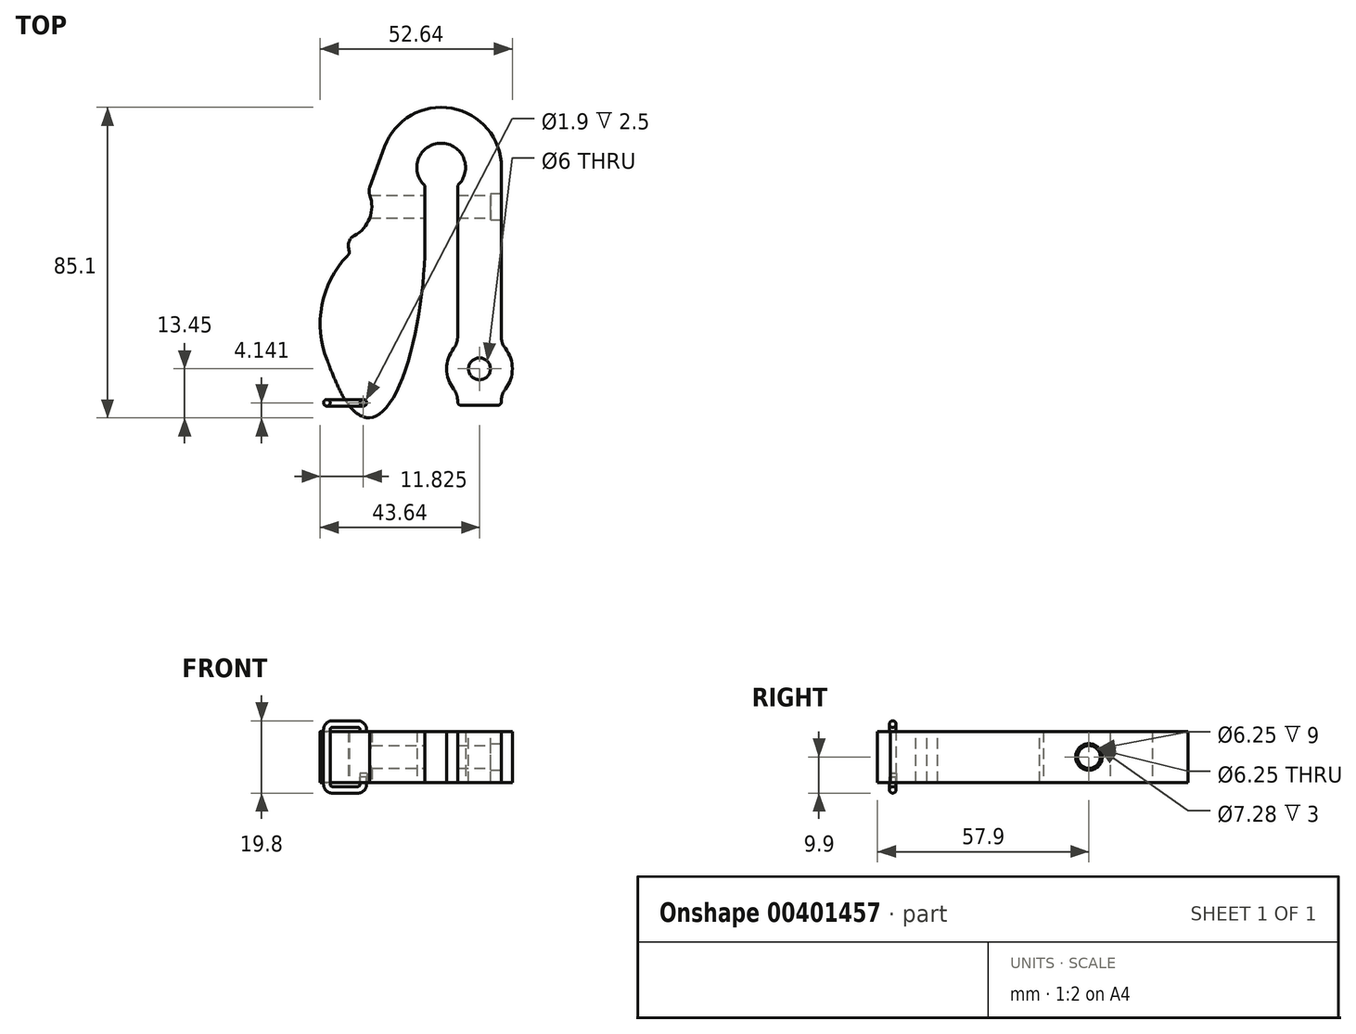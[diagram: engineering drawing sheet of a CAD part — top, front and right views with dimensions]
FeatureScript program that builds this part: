
annotation { "Feature Type Name" : "Feature", "Feature Type Description" : "" }
export const myFeature = defineFeature(function(context is Context, id is Id, definition is map)
    precondition{}
    {
        {
            var Q0;
            Q0=qCreatedBy(makeId("Top.planeOp"),FACE);
            var sketch = newSketch(context, id + "F0", { "sketchPlane" : qUnion([Q0])});
            skCircle(sketch, "E0", {"center": v(0, 0) * mm, "radius": 16.5 * mm, "construction": true});
            skCircle(sketch, "E1", {"center": v(0, 0) * mm, "radius": 6.68 * mm, "construction": true});
            skLineSegment(sketch, "E2.bottom", {"start": v(16.5, 0) * mm, "end": v(4.5, 0) * mm, "construction": true});
            skLineSegment(sketch, "E2.top", {"start": v(16.5, -65.15) * mm, "end": v(4.5, -65.15) * mm, "construction": true});
            skLineSegment(sketch, "E2.left", {"start": v(16.5, 0) * mm, "end": v(16.5, -65.15) * mm, "construction": true});
            skLineSegment(sketch, "E2.right", {"start": v(4.5, 0) * mm, "end": v(4.5, -65.15) * mm, "construction": true});
            skLineSegment(sketch, "E3.bottom", {"start": v(-16.5, 0) * mm, "end": v(-3.67, 0) * mm, "construction": true});
            skLineSegment(sketch, "E4.MirrorCS", {"start": v(-4.5, 0) * mm, "end": v(-4.5, -65.15) * mm, "construction": true});
            skLineSegment(sketch, "E5.MirrorCS", {"start": v(-16.5, 0) * mm, "end": v(-16.5, -65.15) * mm, "construction": true});
            skLineSegment(sketch, "E6.MirrorCS", {"start": v(-16.5, -65.15) * mm, "end": v(-4.5, -65.15) * mm, "construction": true});
            skLineSegment(sketch, "E7", {"start": v(0, 16.5) * mm, "end": v(-40, 16.5) * mm, "construction": true});
            skLineSegment(sketch, "E8", {"start": v(-35.1, 16.5) * mm, "end": v(-35.1, -10.7) * mm, "construction": true});
            skLineSegment(sketch, "E9", {"start": v(-35.1, -10.7) * mm, "end": v(24.91, -10.7) * mm, "construction": true});
            skArc(sketch, "E10", {"start": v(-34.47, -76.44) * mm, "mid": v(-14.3, -71.83) * mm, "end": v(-4.5, -53.6) * mm, "construction": true});
            skPoint(sketch, "E11", {"position": v(-34.47, -76.44) * mm});
            skLineSegment(sketch, "E12", {"start": v(-30, -57) * mm, "end": v(-10.83, -57) * mm, "construction": true});
            skArc(sketch, "E13", {"start": v(-25.7, -24.2) * mm, "mid": v(-32.7, -37.96) * mm, "end": v(-31.02, -53.3) * mm, "construction": true});
            skLineSegment(sketch, "E14", {"start": v(-35.28, -13.7) * mm, "end": v(24.91, -13.7) * mm, "construction": true});
            skLineSegment(sketch, "E15", {"start": v(24.64, -7.7) * mm, "end": v(-35.1, -7.7) * mm, "construction": true});
            skCircle(sketch, "E16", {"center": v(-28, -10.7) * mm, "radius": 9 * mm, "construction": true});
            skLineSegment(sketch, "E17", {"start": v(-20, 5.87) * mm, "end": v(-20, -31.3) * mm, "construction": true});
            skLineSegment(sketch, "E18", {"start": v(-20, -6.58) * mm, "end": v(-15.49, 5.7) * mm, "construction": true});
            skLineSegment(sketch, "E19", {"start": v(-25.7, -15.52) * mm, "end": v(-25.7, -32.88) * mm, "construction": true});
            skLineSegment(sketch, "E20", {"start": v(-37.42, -24.2) * mm, "end": v(-13.09, -24.2) * mm, "construction": true});
            skCircle(sketch, "E21", {"center": v(-60.5, -65.75) * mm, "radius": 32 * mm, "construction": true});
            skPoint(sketch, "E22", {"position": v(-25.7, -24.2) * mm});
            skSolve(sketch);
        }
        {
            var Q0;
            Q0=qCreatedBy(makeId("Top.planeOp"),FACE);
            var sketch = newSketch(context, id + "F1", { "sketchPlane" : qUnion([Q0])});
            skLineSegment(sketch, "E23", {"start": v(-20, -6.58) * mm, "end": v(-15.49, 5.7) * mm});
            skArc(sketch, "E24", {"start": v(-15.49, 5.7) * mm, "mid": v(2.9, 16.24) * mm, "end": v(16.5, 0) * mm});
            skLineSegment(sketch, "E25", {"start": v(16.5, 0) * mm, "end": v(16.5, -65.15) * mm});
            skLineSegment(sketch, "E26", {"start": v(16.5, -65.15) * mm, "end": v(4.5, -65.15) * mm});
            skLineSegment(sketch, "E27", {"start": v(4.5, -65.15) * mm, "end": v(4.5, -4.93) * mm});
            skArc(sketch, "E28", {"start": v(4.5, -4.93) * mm, "mid": v(0, 6.68) * mm, "end": v(-4.5, -4.93) * mm});
            skLineSegment(sketch, "E29", {"start": v(-4.5, -4.93) * mm, "end": v(-4.5, -46.93) * mm});
            skArc(sketch, "E30", {"start": v(-31.18, -52.92) * mm, "mid": v(-32.66, -37.75) * mm, "end": v(-25.7, -24.2) * mm});
            skArc(sketch, "E31", {"start": v(-25.7, -19.4) * mm, "mid": v(-19.78, -14.36) * mm, "end": v(-20, -6.58) * mm});
            skPoint(sketch, "E32", {"position": v(-28.4, -71.45) * mm});
            skArc(sketch, "E33", {"start": v(-28.4, -71.45) * mm, "mid": v(-11.46, -64.05) * mm, "end": v(-4.5, -46.93) * mm});
            skArc(sketch, "E34", {"start": v(-31.18, -52.92) * mm, "mid": v(-28.7, -62.02) * mm, "end": v(-28.4, -71.45) * mm});
            skLineSegment(sketch, "E35", {"start": v(-25.7, -19.4) * mm, "end": v(-25.23, -23.14) * mm});
            skFitSpline(sketch, "E36", {"points": [v(-25.23, -23.14) * mm, v(-25.7, -24.2) * mm], "startDerivative": vector(0.3, -1.7) * mm, "endDerivative": vector(-0.99, -1.09) * mm});
            skSolve(sketch);
        }
        {
            var Q0;
            Q0=makeQuery(id+"F1.imprint","IMPRINT",FACE,{"disambiguationData":[TD([[makeQuery(id+"F1.imprint","IMPRINT",EDGE,{"derivedFrom":sQuery(id+"F1.wireOp",EDGE,"E23")}),-1.0]])]});
            extrude(context, id + "F2", {"entities" : qUnion([Q0]), "depth" : 14 * mm});
        }
        {
            var Q0;
            Q0=makeQuery(id+"F2.opExtrude","SWEPT_FACE",FACE,{"disambiguationData":[OSD([sQuery(id+"F1.wireOp",EDGE,"E25")])]});
            var sketch = newSketch(context, id + "F3", { "sketchPlane" : qUnion([Q0])});
            skCircle(sketch, "E37", {"center": v(-10.7, 7) * mm, "radius": 3.12 * mm});
            skSolve(sketch);
        }
        {
            var Q0;
            Q0=qSketchRegion(id+"F3",true);
            extrude(context, id + "F4", {"entities" : qUnion([Q0]), "operationType" : NewBodyOperationType.REMOVE, "endBound" : BoundingType.THROUGH_ALL, "oppositeDirection" : true, "depth" : 25 * mm});
        }
        {
            var Q0;
            Q0=makeQuery(id+"F2.opExtrude","SWEPT_EDGE",EDGE,{"disambiguationData":[OSD([sQuery(id+"F1.wireOp",EDGE,"iYDEJ3TL-iV67-zqoH-FoCL-mFiRr5Qzbk3r"),sQuery(id+"F1.wireOp",EDGE,"E31")])]});
            fillet(context, id + "F5", {"entities" : qUnion([Q0]), "radius" : 3 * mm, "tangentPropagation" : true, "allowEdgeOverflow" : false});
        }
        {
            var Q0;
            Q0=makeQuery(id+"F2.opExtrude","SWEPT_EDGE",EDGE,{"disambiguationData":[OSD([sQuery(id+"F1.wireOp",EDGE,"E30"),sQuery(id+"F1.wireOp",EDGE,"iYDEJ3TL-iV67-zqoH-FoCL-mFiRr5Qzbk3r")])]});
            fillet(context, id + "F6", {"entities" : qUnion([Q0]), "radius" : 2 * mm, "tangentPropagation" : true, "allowEdgeOverflow" : false});
        }
        {
            var Q0;
            Q0=makeQuery(id+"F2.opExtrude","SWEPT_EDGE",EDGE,{"disambiguationData":[OSD([sQuery(id+"F1.wireOp",EDGE,"E33"),sQuery(id+"F1.wireOp",EDGE,"Xg7VqQur-UJu3-oRoY-WVdC-1TGSa8gNUCBY")])]});
            fillet(context, id + "F7", {"entities" : qUnion([Q0]), "radius" : 5 * mm, "tangentPropagation" : true, "allowEdgeOverflow" : false});
        }
        {
            var Q0;
            Q0=makeQuery(id+"F2.opExtrude","CAP_FACE",FACE,{"disambiguationData":[OSD([sQuery(id+"F1.wireOp",EDGE,"E23"),sQuery(id+"F1.wireOp",EDGE,"E24"),sQuery(id+"F1.wireOp",EDGE,"E25"),sQuery(id+"F1.wireOp",EDGE,"E26"),sQuery(id+"F1.wireOp",EDGE,"E27"),sQuery(id+"F1.wireOp",EDGE,"E28"),sQuery(id+"F1.wireOp",EDGE,"E29"),sQuery(id+"F1.wireOp",EDGE,"E30"),sQuery(id+"F1.wireOp",EDGE,"iYDEJ3TL-iV67-zqoH-FoCL-mFiRr5Qzbk3r"),sQuery(id+"F1.wireOp",EDGE,"E31"),sQuery(id+"F1.wireOp",EDGE,"E33"),sQuery(id+"F1.wireOp",EDGE,"Xg7VqQur-UJu3-oRoY-WVdC-1TGSa8gNUCBY")])],"isStart":false});
            var sketch = newSketch(context, id + "F8", { "sketchPlane" : qUnion([Q0])});
            skCircle(sketch, "E38", {"center": v(10.5, -55.15) * mm, "radius": 3 * mm});
            skPoint(sketch, "E39.middle", {"position": v(10.5, -58.15) * mm});
            skSolve(sketch);
        }
        {
            var Q0;
            Q0=makeQuery(id+"F0fC8d2KKsZCDmL_1.boolean.opBoolean","COPY",EDGE,{"derivedFrom":makeQuery(id+"F0fC8d2KKsZCDmL_1.opExtrude","CAP_EDGE",EDGE,{"disambiguationData":[OSD([sQuery(id+"F8.wireOp",EDGE,"E39.left")])],"isStart":true})});
            var Q1;
            Q1=makeQuery(id+"F0fC8d2KKsZCDmL_1.boolean.opBoolean","COPY",EDGE,{"derivedFrom":makeQuery(id+"F0fC8d2KKsZCDmL_1.opExtrude","CAP_EDGE",EDGE,{"disambiguationData":[OSD([sQuery(id+"F8.wireOp",EDGE,"E38")])],"isStart":true})});
            var Q2;
            Q2=makeQuery(id+"F2.opExtrude","SWEPT_EDGE",EDGE,{"disambiguationData":[OSD([sQuery(id+"F1.wireOp",EDGE,"E26"),sQuery(id+"F1.wireOp",EDGE,"E27")])]});
            var Q3;
            Q3=makeQuery(id+"F2.opExtrude","SWEPT_EDGE",EDGE,{"disambiguationData":[OSD([sQuery(id+"F1.wireOp",EDGE,"E25"),sQuery(id+"F1.wireOp",EDGE,"E26")])]});
            var Q4;
            Q4=makeQuery(id+"F0fC8d2KKsZCDmL_1.boolean.opBoolean","INTERSECT",EDGE,{"derivedFrom":[makeQuery(id+"F2.opExtrude","CAP_FACE",FACE,{"disambiguationData":[OSD([sQuery(id+"F1.wireOp",EDGE,"E23"),sQuery(id+"F1.wireOp",EDGE,"E24"),sQuery(id+"F1.wireOp",EDGE,"E25"),sQuery(id+"F1.wireOp",EDGE,"E26"),sQuery(id+"F1.wireOp",EDGE,"E27"),sQuery(id+"F1.wireOp",EDGE,"E28"),sQuery(id+"F1.wireOp",EDGE,"E29"),sQuery(id+"F1.wireOp",EDGE,"E30"),sQuery(id+"F1.wireOp",EDGE,"iYDEJ3TL-iV67-zqoH-FoCL-mFiRr5Qzbk3r"),sQuery(id+"F1.wireOp",EDGE,"E31"),sQuery(id+"F1.wireOp",EDGE,"E33"),sQuery(id+"F1.wireOp",EDGE,"Xg7VqQur-UJu3-oRoY-WVdC-1TGSa8gNUCBY")])],"isStart":true}),makeQuery(id+"F0fC8d2KKsZCDmL_1.opExtrude","SWEPT_FACE",FACE,{"disambiguationData":[OSD([sQuery(id+"F8.wireOp",EDGE,"E39.right")])]})]});
            fillet(context, id + "F9", {"entities" : qUnion([Q0, Q1, Q2, Q3, Q4]), "radius" : 1 * mm, "tangentPropagation" : true, "allowEdgeOverflow" : false});
        }
        {
            var Q0;
            Q0=qCreatedBy(makeId("Top.planeOp"),FACE);
            var sketch = newSketch(context, id + "F10", { "sketchPlane" : qUnion([Q0])});
            skLineSegment(sketch, "E40", {"start": v(-5.9, -69.53) * mm, "end": v(-56.37, -69.53) * mm, "construction": true});
            skLineSegment(sketch, "E41", {"start": v(-56.43, -70.53) * mm, "end": v(-5.7, -70.53) * mm, "construction": true});
            skLineSegment(sketch, "E42", {"start": v(-27.31, -50.14) * mm, "end": v(-27.31, -74.97) * mm, "construction": true});
            skLineSegment(sketch, "E43", {"start": v(-28.31, -50.14) * mm, "end": v(-28.31, -74.79) * mm, "construction": true});
            skLineSegment(sketch, "E44", {"start": v(-21.31, -51.33) * mm, "end": v(-21.31, -64.46) * mm, "construction": true});
            skLineSegment(sketch, "E45", {"start": v(-32.6, -67.53) * mm, "end": v(-13.03, -67.53) * mm, "construction": true});
            skCircle(sketch, "E46", {"center": v(-21.31, -64.46) * mm, "radius": 0.95 * mm});
            skArc(sketch, "E47", {"start": v(-29.98, -59.47) * mm, "mid": v(-25, -73.75) * mm, "end": v(-11.59, -66.78) * mm, "construction": true});
            skSolve(sketch);
        }
        {
            var Q0;
            Q0=qSketchRegion(id+"F10",true);
            extrude(context, id + "F11", {"entities" : qUnion([Q0]), "operationType" : NewBodyOperationType.REMOVE, "depth" : 1.5 * mm});
        }
        {
            var Q0;
            Q0=makeQuery(id+"F2.opExtrude","CAP_FACE",FACE,{"disambiguationData":[OSD([sQuery(id+"F1.wireOp",EDGE,"E23"),sQuery(id+"F1.wireOp",EDGE,"E24"),sQuery(id+"F1.wireOp",EDGE,"E25"),sQuery(id+"F1.wireOp",EDGE,"E26"),sQuery(id+"F1.wireOp",EDGE,"E27"),sQuery(id+"F1.wireOp",EDGE,"E28"),sQuery(id+"F1.wireOp",EDGE,"E29"),sQuery(id+"F1.wireOp",EDGE,"E30"),sQuery(id+"F1.wireOp",EDGE,"iYDEJ3TL-iV67-zqoH-FoCL-mFiRr5Qzbk3r"),sQuery(id+"F1.wireOp",EDGE,"E31"),sQuery(id+"F1.wireOp",EDGE,"E33"),sQuery(id+"F1.wireOp",EDGE,"Xg7VqQur-UJu3-oRoY-WVdC-1TGSa8gNUCBY")])],"isStart":false});
            var sketch = newSketch(context, id + "F12", { "sketchPlane" : qUnion([Q0])});
            skCircle(sketch, "E48", {"center": v(-21.31, -64.46) * mm, "radius": 0.9 * mm});
            skSolve(sketch);
        }
        {
            var Q0;
            Q0=qSketchRegion(id+"F12",true);
            extrude(context, id + "F13", {"entities" : qUnion([Q0]), "operationType" : NewBodyOperationType.REMOVE, "oppositeDirection" : true, "depth" : 2.5 * mm});
        }
        {
            var Q0;
            Q0=makeQuery(id+"F2.opExtrude","CAP_FACE",FACE,{"disambiguationData":[OSD([sQuery(id+"F1.wireOp",EDGE,"E23"),sQuery(id+"F1.wireOp",EDGE,"E24"),sQuery(id+"F1.wireOp",EDGE,"E25"),sQuery(id+"F1.wireOp",EDGE,"E26"),sQuery(id+"F1.wireOp",EDGE,"E27"),sQuery(id+"F1.wireOp",EDGE,"E28"),sQuery(id+"F1.wireOp",EDGE,"E29"),sQuery(id+"F1.wireOp",EDGE,"E30"),sQuery(id+"F1.wireOp",EDGE,"iYDEJ3TL-iV67-zqoH-FoCL-mFiRr5Qzbk3r"),sQuery(id+"F1.wireOp",EDGE,"E31"),sQuery(id+"F1.wireOp",EDGE,"E33"),sQuery(id+"F1.wireOp",EDGE,"Xg7VqQur-UJu3-oRoY-WVdC-1TGSa8gNUCBY")])],"isStart":false});
            cPlane(context, id + "F14", {"entities" : qUnion([Q0]), "cplaneType" : CPlaneType.OFFSET, "offset" : 4 * mm, "oppositeDirection" : true, "width" : 150 * mm, "height" : 150 * mm});
        }
        {
            var Q0;
            Q0=qCreatedBy(id+"F14.planeOp",FACE);
            cPlane(context, id + "F15", {"entities" : qUnion([Q0]), "cplaneType" : CPlaneType.OFFSET, "offset" : 6 * mm, "oppositeDirection" : true, "width" : 150 * mm, "height" : 150 * mm});
        }
        {
            var Q0;
            Q0=makeQuery(id+"F3.imprint","IMPRINT",FACE,{"disambiguationData":[TD([[makeQuery(id+"F3.imprint","IMPRINT",EDGE,{"derivedFrom":sQuery(id+"F3.wireOp",EDGE,"E37")}),-1.0]])]});
            var sketch = newSketch(context, id + "F16", { "sketchPlane" : qUnion([Q0])});
            skCircle(sketch, "E49", {"center": v(-10.7, 7) * mm, "radius": 3.64 * mm});
            skSolve(sketch);
        }
        {
            var Q0;
            Q0=qSketchRegion(id+"F16",true);
            extrude(context, id + "F17", {"entities" : qUnion([Q0]), "operationType" : NewBodyOperationType.REMOVE, "oppositeDirection" : true, "depth" : 3 * mm});
        }
        {
            var Q0;
            Q0=makeQuery(id+"F2.opExtrude","CAP_FACE",FACE,{"disambiguationData":[OSD([sQuery(id+"F1.wireOp",EDGE,"E23"),sQuery(id+"F1.wireOp",EDGE,"E24"),sQuery(id+"F1.wireOp",EDGE,"E25"),sQuery(id+"F1.wireOp",EDGE,"E26"),sQuery(id+"F1.wireOp",EDGE,"E27"),sQuery(id+"F1.wireOp",EDGE,"E28"),sQuery(id+"F1.wireOp",EDGE,"E29"),sQuery(id+"F1.wireOp",EDGE,"E30"),sQuery(id+"F1.wireOp",EDGE,"iYDEJ3TL-iV67-zqoH-FoCL-mFiRr5Qzbk3r"),sQuery(id+"F1.wireOp",EDGE,"E31"),sQuery(id+"F1.wireOp",EDGE,"E33"),sQuery(id+"F1.wireOp",EDGE,"E34")])],"isStart":false});
            var sketch = newSketch(context, id + "F18", { "sketchPlane" : qUnion([Q0])});
            skFitSpline(sketch, "E50", {"points": [v(-30.37, -55.1) * mm, v(-24.1, -66.53) * mm, v(-14.21, -66.47) * mm], "startDerivative": vector(8.93, -20.6) * mm, "endDerivative": vector(25.63, 20.5) * mm});
            skLineSegment(sketch, "E51", {"start": v(-30.37, -55.1) * mm, "end": v(-30.37, -71.38) * mm});
            skLineSegment(sketch, "E52", {"start": v(-30.37, -71.38) * mm, "end": v(-14.21, -71.38) * mm});
            skLineSegment(sketch, "E53", {"start": v(-14.21, -71.38) * mm, "end": v(-14.21, -66.47) * mm});
            skSolve(sketch);
        }
        {
            var Q0;
            Q0=qSketchRegion(id+"F18",true);
            extrude(context, id + "F19", {"entities" : qUnion([Q0]), "operationType" : NewBodyOperationType.REMOVE, "endBound" : BoundingType.THROUGH_ALL, "oppositeDirection" : true, "depth" : 25 * mm});
        }
        {
            var Q0;
            Q0=makeQuery(id+"F2.opExtrude","CAP_FACE",FACE,{"disambiguationData":[OSD([sQuery(id+"F1.wireOp",EDGE,"E23"),sQuery(id+"F1.wireOp",EDGE,"E24"),sQuery(id+"F1.wireOp",EDGE,"E25"),sQuery(id+"F1.wireOp",EDGE,"E26"),sQuery(id+"F1.wireOp",EDGE,"E27"),sQuery(id+"F1.wireOp",EDGE,"E28"),sQuery(id+"F1.wireOp",EDGE,"E29"),sQuery(id+"F1.wireOp",EDGE,"E30"),sQuery(id+"F1.wireOp",EDGE,"iYDEJ3TL-iV67-zqoH-FoCL-mFiRr5Qzbk3r"),sQuery(id+"F1.wireOp",EDGE,"E31"),sQuery(id+"F1.wireOp",EDGE,"E33"),sQuery(id+"F1.wireOp",EDGE,"E34")])],"isStart":false});
            var sketch = newSketch(context, id + "F20", { "sketchPlane" : qUnion([Q0])});
            skCircle(sketch, "E54", {"center": v(10.5, -55.15) * mm, "radius": 9 * mm});
            skSolve(sketch);
        }
        {
            var Q0;
            Q0=qSketchRegion(id+"F20",true);
            extrude(context, id + "F21", {"entities" : qUnion([Q0]), "operationType" : NewBodyOperationType.ADD, "oppositeDirection" : true, "depth" : 14 * mm});
        }
        {
            var Q0;
            Q0=makeQuery(id+"F21.boolean.opBoolean","INTERSECT",EDGE,{"disambiguationData":[OD(1.0)],"derivedFrom":[makeQuery(id+"F2.opExtrude","SWEPT_FACE",FACE,{"disambiguationData":[OSD([sQuery(id+"F1.wireOp",EDGE,"E25")])]}),makeQuery(id+"F21.opExtrude","SWEPT_FACE",FACE,{"disambiguationData":[OSD([sQuery(id+"F20.wireOp",EDGE,"E54")])]})]});
            var Q1;
            Q1=makeQuery(id+"F21.boolean.opBoolean","INTERSECT",EDGE,{"disambiguationData":[OD(0.0)],"derivedFrom":[makeQuery(id+"F2.opExtrude","SWEPT_FACE",FACE,{"disambiguationData":[OSD([sQuery(id+"F1.wireOp",EDGE,"E25")])]}),makeQuery(id+"F21.opExtrude","SWEPT_FACE",FACE,{"disambiguationData":[OSD([sQuery(id+"F20.wireOp",EDGE,"E54")])]})]});
            var Q2;
            Q2=makeQuery(id+"F21.boolean.opBoolean","INTERSECT",EDGE,{"disambiguationData":[OD(1.0)],"derivedFrom":[makeQuery(id+"F2.opExtrude","SWEPT_FACE",FACE,{"disambiguationData":[OSD([sQuery(id+"F1.wireOp",EDGE,"E27")])]}),makeQuery(id+"F21.opExtrude","SWEPT_FACE",FACE,{"disambiguationData":[OSD([sQuery(id+"F20.wireOp",EDGE,"E54")])]})]});
            var Q3;
            Q3=makeQuery(id+"F21.boolean.opBoolean","INTERSECT",EDGE,{"disambiguationData":[OD(0.0)],"derivedFrom":[makeQuery(id+"F2.opExtrude","SWEPT_FACE",FACE,{"disambiguationData":[OSD([sQuery(id+"F1.wireOp",EDGE,"E27")])]}),makeQuery(id+"F21.opExtrude","SWEPT_FACE",FACE,{"disambiguationData":[OSD([sQuery(id+"F20.wireOp",EDGE,"E54")])]})]});
            fillet(context, id + "F22", {"entities" : qUnion([Q0, Q1, Q2, Q3]), "radius" : 5 * mm, "tangentPropagation" : true, "allowEdgeOverflow" : false});
        }
        {
            var Q0;
            Q0=makeQuery(id+"F1.imprint","IMPRINT",FACE,{"disambiguationData":[TD([[makeQuery(id+"F1.imprint","IMPRINT",EDGE,{"derivedFrom":sQuery(id+"F1.wireOp",EDGE,"E23")}),-1.0]])]});
            var sketch = newSketch(context, id + "F23", { "sketchPlane" : qUnion([Q0])});
            skFitSpline(sketch, "E55", {"points": [v(-18.29, -68.5) * mm, v(-15.6, -67.31) * mm, v(-13.16, -65.61) * mm], "startDerivative": vector(5.8, 1.03) * mm, "endDerivative": vector(4.69, 3.67) * mm});
            skSolve(sketch);
        }
        {
            var Q0;
            Q0=makeQuery(id+"F21.boolean.opBoolean","MERGE",FACE,{"derivedFrom":[makeQuery(id+"F2.opExtrude","CAP_FACE",FACE,{"disambiguationData":[OSD([sQuery(id+"F1.wireOp",EDGE,"E23"),sQuery(id+"F1.wireOp",EDGE,"E24"),sQuery(id+"F1.wireOp",EDGE,"E25"),sQuery(id+"F1.wireOp",EDGE,"E26"),sQuery(id+"F1.wireOp",EDGE,"E27"),sQuery(id+"F1.wireOp",EDGE,"E28"),sQuery(id+"F1.wireOp",EDGE,"E29"),sQuery(id+"F1.wireOp",EDGE,"E30"),sQuery(id+"F1.wireOp",EDGE,"iYDEJ3TL-iV67-zqoH-FoCL-mFiRr5Qzbk3r"),sQuery(id+"F1.wireOp",EDGE,"E31"),sQuery(id+"F1.wireOp",EDGE,"E33"),sQuery(id+"F1.wireOp",EDGE,"E34")])],"isStart":false}),makeQuery(id+"F21.opExtrude","CAP_FACE",FACE,{"disambiguationData":[OSD([sQuery(id+"F20.wireOp",EDGE,"E54")])],"isStart":true})]});
            var sketch = newSketch(context, id + "F24", { "sketchPlane" : qUnion([Q0])});
            skFitSpline(sketch, "E56", {"points": [v(-19.6, -68.6) * mm, v(-12.63, -62.2) * mm, v(-4.5, -24.2) * mm], "startDerivative": vector(19.29, 1.25) * mm, "endDerivative": vector(1.65, 57) * mm});
            skPoint(sketch, "E57", {"position": v(-4.5, -25.93) * mm});
            skPoint(sketch, "E58", {"position": v(-25.7, -24.2) * mm});
            skLineSegment(sketch, "E59", {"start": v(-19.58, -68.6) * mm, "end": v(-19.58, -69.61) * mm});
            skLineSegment(sketch, "E60", {"start": v(-19.58, -69.61) * mm, "end": v(-2.42, -69.61) * mm});
            skLineSegment(sketch, "E61", {"start": v(-2.42, -69.61) * mm, "end": v(-2.42, -24.2) * mm});
            skLineSegment(sketch, "E62", {"start": v(-2.42, -24.2) * mm, "end": v(-4.5, -24.2) * mm});
            skSolve(sketch);
        }
        {
            var Q0;
            Q0=qSketchRegion(id+"F24",true);
            extrude(context, id + "F25", {"entities" : qUnion([Q0]), "operationType" : NewBodyOperationType.REMOVE, "endBound" : BoundingType.THROUGH_ALL, "oppositeDirection" : true, "depth" : 25 * mm});
        }
        {
            var Q0;
            Q0=makeQuery(id+"F8.imprint","IMPRINT",FACE,{"disambiguationData":[TD([[makeQuery(id+"F8.imprint","IMPRINT",EDGE,{"derivedFrom":sQuery(id+"F8.wireOp",EDGE,"E38")}),1.0]])]});
            extrude(context, id + "F26", {"entities" : qUnion([Q0]), "operationType" : NewBodyOperationType.REMOVE, "endBound" : BoundingType.THROUGH_ALL, "oppositeDirection" : true, "depth" : 25 * mm});
        }
        {
            var Q0;
            Q0=makeQuery(id+"F23.imprint","IMPRINT",FACE,{"disambiguationData":[TD([[makeQuery(id+"F23.imprint","IMPRINT",EDGE,{"derivedFrom":makeQuery(id+"F1.imprint","IMPRINT",EDGE,{"derivedFrom":sQuery(id+"F1.wireOp",EDGE,"E23")})}),-1.0]])]});
            var sketch = newSketch(context, id + "F27", { "sketchPlane" : qUnion([Q0])});
            skCircle(sketch, "E63", {"center": v(-21.31, -64.46) * mm, "radius": 0.95 * mm});
            skSolve(sketch);
        }
        {
            var Q0;
            Q0=qSketchRegion(id+"F27",true);
            extrude(context, id + "F28", {"entities" : qUnion([Q0]), "operationType" : NewBodyOperationType.REMOVE, "depth" : 2.5 * mm});
        }
        {
            var Q0;
            Q0=qCreatedBy(makeId("Front.planeOp"),FACE);
            cPlane(context, id + "F29", {"entities" : qUnion([Q0]), "cplaneType" : CPlaneType.OFFSET, "offset" : 64.46 * mm, "width" : 150 * mm, "height" : 150 * mm});
        }
        {
            var Q0;
            Q0=qCreatedBy(id+"F29.planeOp",FACE);
            var sketch = newSketch(context, id + "F30", { "sketchPlane" : qUnion([Q0])});
            skLineSegment(sketch, "E64.bottom", {"start": v(-21.31, 16) * mm, "end": v(-31.31, 16) * mm, "construction": true});
            skLineSegment(sketch, "E64.top", {"start": v(-21.31, -2) * mm, "end": v(-31.31, -2) * mm, "construction": true});
            skLineSegment(sketch, "E64.left", {"start": v(-21.31, 16) * mm, "end": v(-21.31, -2) * mm, "construction": true});
            skLineSegment(sketch, "E64.right", {"start": v(-31.31, 16) * mm, "end": v(-31.31, -2) * mm, "construction": true});
            skPoint(sketch, "E64.middle", {"position": v(-26.31, 7) * mm});
            skSolve(sketch);
        }
        {
            var Q0;
            Q0=qCreatedBy(id+"F29.planeOp",FACE);
            var sketch = newSketch(context, id + "F31", { "sketchPlane" : qUnion([Q0])});
            skLineSegment(sketch, "E65", {"start": v(-22.81, 16) * mm, "end": v(-29.81, 16) * mm});
            skLineSegment(sketch, "E66", {"start": v(-31.31, 14.5) * mm, "end": v(-31.31, -0.5) * mm});
            skLineSegment(sketch, "E67", {"start": v(-29.81, -2) * mm, "end": v(-22.81, -2) * mm});
            skPoint(sketch, "E68.visualSharp", {"position": v(-31.31, -2) * mm});
            skArc(sketch, "E68.filletArc", {"start": v(-31.31, -0.5) * mm, "mid": v(-30.88, -1.56) * mm, "end": v(-29.81, -2) * mm});
            skPoint(sketch, "E69.visualSharp", {"position": v(-31.31, 16) * mm});
            skArc(sketch, "E69.filletArc", {"start": v(-29.81, 16) * mm, "mid": v(-30.88, 15.56) * mm, "end": v(-31.31, 14.5) * mm});
            skLineSegment(sketch, "E70", {"start": v(-21.31, 14.5) * mm, "end": v(-21.31, 12.5) * mm});
            skLineSegment(sketch, "E71", {"start": v(-21.31, -0.5) * mm, "end": v(-21.31, 1.5) * mm});
            skPoint(sketch, "E72.visualSharp", {"position": v(-21.31, 16) * mm});
            skArc(sketch, "E72.filletArc", {"start": v(-21.31, 14.5) * mm, "mid": v(-21.75, 15.56) * mm, "end": v(-22.81, 16) * mm});
            skPoint(sketch, "E73.visualSharp", {"position": v(-21.31, -2) * mm});
            skArc(sketch, "E73.filletArc", {"start": v(-22.81, -2) * mm, "mid": v(-21.75, -1.56) * mm, "end": v(-21.31, -0.5) * mm});
            skSolve(sketch);
        }
        {
            var Q0;
            Q0=makeQuery(id+"F13.boolean.opBoolean","COPY",FACE,{"derivedFrom":makeQuery(id+"F13.opExtrude","CAP_FACE",FACE,{"disambiguationData":[OSD([sQuery(id+"F12.wireOp",EDGE,"E48")])],"isStart":false})});
            cPlane(context, id + "F32", {"entities" : qUnion([Q0]), "cplaneType" : CPlaneType.OFFSET, "offset" : 1 * mm, "width" : 150 * mm, "height" : 150 * mm});
        }
        {
            var Q0;
            Q0=qCreatedBy(id+"F32.planeOp",FACE);
            var sketch = newSketch(context, id + "F33", { "sketchPlane" : qUnion([Q0])});
            skCircle(sketch, "E74", {"center": v(-21.31, -64.46) * mm, "radius": 0.9 * mm});
            skSolve(sketch);
        }
        {
            var Q0;
            Q0=qSketchRegion(id+"F33",true);
            var Q1;
            Q1=sQuery(id+"F31.wireOp",EDGE,"E70");
            var Q2;
            Q2=sQuery(id+"F31.wireOp",EDGE,"E72.filletArc");
            var Q3;
            Q3=sQuery(id+"F31.wireOp",EDGE,"E65");
            var Q4;
            Q4=sQuery(id+"F31.wireOp",EDGE,"E69.filletArc");
            var Q5;
            Q5=sQuery(id+"F31.wireOp",EDGE,"E66");
            var Q6;
            Q6=sQuery(id+"F31.wireOp",EDGE,"E68.filletArc");
            var Q7;
            Q7=sQuery(id+"F31.wireOp",EDGE,"E67");
            var Q8;
            Q8=sQuery(id+"F31.wireOp",EDGE,"E73.filletArc");
            var Q9;
            Q9=sQuery(id+"F31.wireOp",EDGE,"E71");
            sweep(context, id + "F34", {"profiles" : qUnion([Q0]), "path" : qUnion([Q1, Q2, Q3, Q4, Q5, Q6, Q7, Q8, Q9])});
        }
        {
            var Q0;
            Q0=qCreatedBy(makeId("Top.planeOp"),FACE);
            cPlane(context, id + "F35", {"entities" : qUnion([Q0]), "cplaneType" : CPlaneType.OFFSET, "offset" : 12.5 * mm, "width" : 150 * mm, "height" : 150 * mm});
        }
        {
            var Q0;
            Q0=qCreatedBy(id+"F35.planeOp",FACE);
            var sketch = newSketch(context, id + "F36", { "sketchPlane" : qUnion([Q0])});
            skCircle(sketch, "E75", {"center": v(-21.31, -64.46) * mm, "radius": 0.9 * mm});
            skSolve(sketch);
        }
        {
            var Q0;
            Q0=qSketchRegion(id+"F36",true);
            extrude(context, id + "F37", {"entities" : qUnion([Q0]), "operationType" : NewBodyOperationType.ADD, "oppositeDirection" : true, "depth" : 1.5 * mm});
        }
    });
